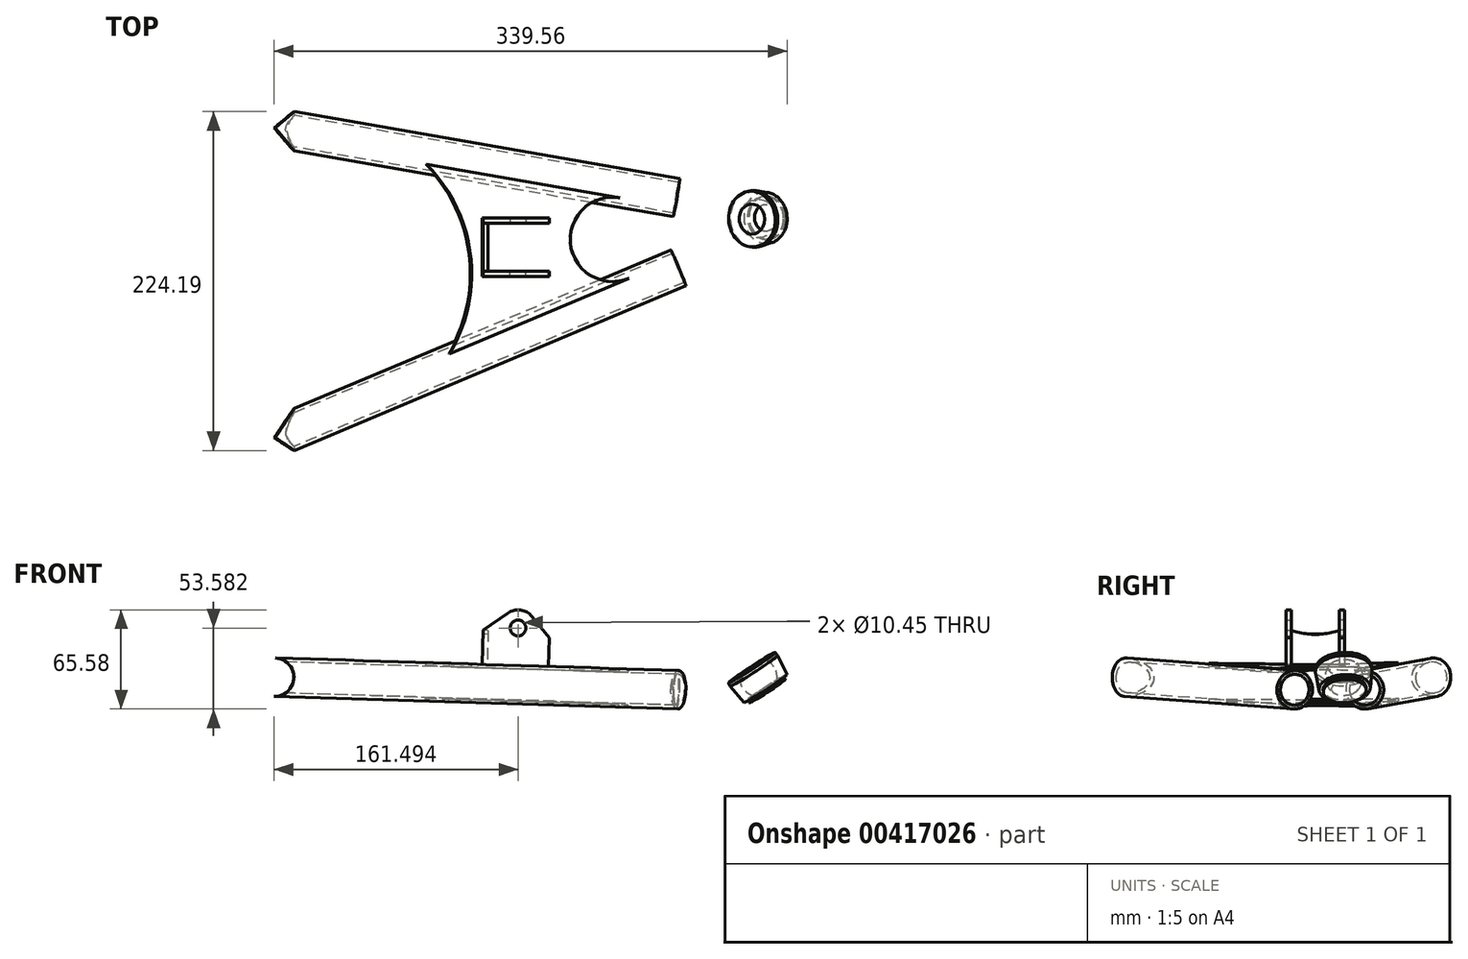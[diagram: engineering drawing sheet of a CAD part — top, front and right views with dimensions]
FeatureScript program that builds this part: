
annotation { "Feature Type Name" : "Feature", "Feature Type Description" : "" }
export const myFeature = defineFeature(function(context is Context, id is Id, definition is map)
    precondition{}
    {
        {
            var Q0;
            Q0=qCreatedBy(makeId("Front.planeOp"),FACE);
            var sketch = newSketch(context, id + "F0", { "sketchPlane" : qUnion([Q0])});
            skLineSegment(sketch, "E0", {"start": v(0, 0) * mm, "end": v(319.69, -10) * mm});
            skLineSegment(sketch, "E1", {"start": v(319.69, -10) * mm, "end": v(320, 0) * mm});
            skLineSegment(sketch, "E2", {"start": v(159.92, -5) * mm, "end": v(161.1, 32.48) * mm, "construction": true});
            skSolve(sketch);
        }
        {
            var Q0;
            Q0=qCreatedBy(makeId("Front.planeOp"),FACE);
            var Q1;
            Q1=sQuery(id+"F0.wireOp",EDGE,"E0");
            cPlane(context, id + "F1", {"entities" : qUnion([Q0, Q1]), "cplaneType" : CPlaneType.LINE_ANGLE, "offset" : 25.4 * mm, "angle" : 90 * degree, "width" : 152.4 * mm, "height" : 152.4 * mm});
        }
        {
            var Q0;
            Q0=qCreatedBy(id+"F1.planeOp",FACE);
            var sketch = newSketch(context, id + "F2", { "sketchPlane" : qUnion([Q0])});
            skLineSegment(sketch, "E3", {"start": v(0, 60) * mm, "end": v(266, 13.74) * mm});
            skLineSegment(sketch, "E4", {"start": v(345, 0) * mm, "end": v(267.35, -32.64) * mm, "construction": true});
            skLineSegment(sketch, "E5", {"start": v(266, 13.74) * mm, "end": v(345, 0) * mm, "construction": true});
            skLineSegment(sketch, "E6", {"start": v(267.35, -32.64) * mm, "end": v(0, -145) * mm});
            skLineSegment(sketch, "E7", {"start": v(0, 81) * mm, "end": v(0, 32) * mm});
            skLineSegment(sketch, "E8", {"start": v(0, -161) * mm, "end": v(0, -112) * mm});
            skLineSegment(sketch, "E9", {"start": v(160, -3) * mm, "end": v(160, -35) * mm, "construction": true});
            skLineSegment(sketch, "E10", {"start": v(160, -19) * mm, "end": v(41.18, -19) * mm, "construction": true});
            skSolve(sketch);
        }
        {
            var Q0;
            Q0=qCreatedBy(makeId("Top.planeOp"),FACE);
            var sketch = newSketch(context, id + "F3", { "sketchPlane" : qUnion([Q0])});
            skLineSegment(sketch, "E11", {"start": v(319.09, 10.43) * mm, "end": v(320.91, -10.43) * mm});
            skSolve(sketch);
        }
        {
            var Q0;
            Q0=qCreatedBy(makeId("Top.planeOp"),FACE);
            var Q1;
            Q1=sQuery(id+"F3.wireOp",EDGE,"E11");
            cPlane(context, id + "F4", {"entities" : qUnion([Q0, Q1]), "cplaneType" : CPlaneType.LINE_ANGLE, "offset" : 25.4 * mm, "angle" : 33 * degree, "width" : 152.4 * mm, "height" : 152.4 * mm});
        }
        {
            var Q0;
            Q0=qCreatedBy(id+"F4.planeOp",FACE);
            var sketch = newSketch(context, id + "F5", { "sketchPlane" : qUnion([Q0])});
            skLineSegment(sketch, "E12", {"start": v(280.63, -1.23) * mm, "end": v(256.98, 1.23) * mm});
            skSolve(sketch);
        }
        {
            var Q0;
            Q0=qCreatedBy(id+"F4.planeOp",FACE);
            var Q1;
            Q1 = qBodyType(qCreatedBy(id + "F5" ,EDGE), BodyType.WIRE);
            cPlane(context, id + "F6", {"entities" : qUnion([Q0, Q1]), "cplaneType" : CPlaneType.LINE_ANGLE, "offset" : 25.4 * mm, "angle" : 90 * degree, "width" : 152.4 * mm, "height" : 152.4 * mm});
        }
        {
            var Q0;
            Q0=qCreatedBy(id+"F6.planeOp",FACE);
            var sketch = newSketch(context, id + "F7", { "sketchPlane" : qUnion([Q0])});
            skLineSegment(sketch, "E13", {"start": v(-312.78, 9.24) * mm, "end": v(-324.78, -9.24) * mm, "construction": true});
            skLineSegment(sketch, "E14", {"start": v(-324.77, -9.23) * mm, "end": v(-336.72, -1.46) * mm});
            skLineSegment(sketch, "E15", {"start": v(-336.72, -1.46) * mm, "end": v(-335.64, 0.21) * mm});
            skLineSegment(sketch, "E16", {"start": v(-335.64, 0.21) * mm, "end": v(-337.94, 1.71) * mm});
            skLineSegment(sketch, "E17", {"start": v(-337.94, 1.71) * mm, "end": v(-331.76, 14.39) * mm});
            skLineSegment(sketch, "E18", {"start": v(-331.76, 14.39) * mm, "end": v(-330.14, 16.32) * mm});
            skLineSegment(sketch, "E19", {"start": v(-330.14, 16.32) * mm, "end": v(-323.08, 11.74) * mm});
            skArc(sketch, "E20", {"start": v(-323.08, 11.74) * mm, "mid": v(-329.78, 5.95) * mm, "end": v(-330.96, -2.82) * mm});
            skLineSegment(sketch, "E21", {"start": v(-330.96, -2.82) * mm, "end": v(-323.68, -7.55) * mm});
            skLineSegment(sketch, "E22", {"start": v(-323.68, -7.55) * mm, "end": v(-324.77, -9.23) * mm});
            skSolve(sketch);
        }
        {
            var Q0;
            Q0=makeQuery(id+"F7.imprint","IMPRINT",FACE,{"disambiguationData":[TD([[makeQuery(id+"F7.imprint","IMPRINT",EDGE,{"derivedFrom":sQuery(id+"F7.wireOp",EDGE,"E14")}),-1.0]])]});
            var Q1;
            Q1=sQuery(id+"F7.wireOp",EDGE,"E13");
            revolve(context, id + "F8", {"entities" : qUnion([Q0]), "axis" : qUnion([Q1]), "revolveType" : RevolveType.FULL});
        }
        {
            var Q0;
            Q0=qCreatedBy(makeId("Front.planeOp"),FACE);
            var sketch = newSketch(context, id + "F9", { "sketchPlane" : qUnion([Q0])});
            skCircle(sketch, "E23", {"center": v(0, 0) * mm, "radius": 12.75 * mm});
            skCircle(sketch, "E24", {"center": v(0, 0) * mm, "radius": 10.5 * mm});
            skLineSegment(sketch, "E25", {"start": v(24, 12) * mm, "end": v(188.38, 6.87) * mm, "construction": true});
            skLineSegment(sketch, "E26", {"start": v(24.34, -13.52) * mm, "end": v(189.13, -18.67) * mm, "construction": true});
            skSolve(sketch);
        }
        {
            var Q0;
            Q0 = qSketchRegion(id + "F9", true);
            var Q1;
            Q1=sQuery(id+"F2.wireOp",VERTEX,"E8.start");
            var Q2;
            Q2=sQuery(id+"F2.wireOp",VERTEX,"E7.start");
            extrude(context, id + "F10", {"entities" : qUnion([Q0]), "endBound" : BoundingType.UP_TO_VERTEX, "endBoundEntityVertex" : qUnion([Q1]), "depth" : 25.4 * mm, "hasSecondDirection" : true, "secondDirectionBound" : BoundingType.UP_TO_VERTEX, "secondDirectionOppositeDirection" : true, "secondDirectionBoundEntityVertex" : qUnion([Q2]), "secondDirectionDepth" : 25.4 * mm});
        }
        {
            var Q0;
            Q0=qCreatedBy(makeId("Top.planeOp"),FACE);
            var sketch = newSketch(context, id + "F11", { "sketchPlane" : qUnion([Q0])});
            skLineSegment(sketch, "E27.bottom", {"start": v(-116.55, 32) * mm, "end": v(116.55, 32) * mm});
            skLineSegment(sketch, "E27.top", {"start": v(-116.55, -112) * mm, "end": v(116.55, -112) * mm});
            skLineSegment(sketch, "E27.left", {"start": v(-116.55, 32) * mm, "end": v(-116.55, -112) * mm});
            skLineSegment(sketch, "E27.right", {"start": v(116.55, 32) * mm, "end": v(116.55, -112) * mm});
            skSolve(sketch);
        }
        {
            var Q0;
            Q0 = qSketchRegion(id + "F11", true);
            extrude(context, id + "F12", {"entities" : qUnion([Q0]), "operationType" : NewBodyOperationType.REMOVE, "endBound" : BoundingType.THROUGH_ALL, "oppositeDirection" : true, "depth" : 25.4 * mm, "hasSecondDirection" : true, "secondDirectionBound" : BoundingType.THROUGH_ALL, "secondDirectionOppositeDirection" : false, "secondDirectionDepth" : 25.4 * mm});
        }
        {
            var Q0;
            Q0=sQuery(id+"F2.wireOp",EDGE,"E3");
            var Q1;
            Q1=sQuery(id+"F2.wireOp",VERTEX,"E3.start");
            cPlane(context, id + "F13", {"entities" : qUnion([Q0, Q1]), "cplaneType" : CPlaneType.LINE_POINT, "offset" : 25.4 * mm, "width" : 152.4 * mm, "height" : 152.4 * mm});
        }
        {
            var Q0;
            Q0=qCreatedBy(id+"F13.planeOp",FACE);
            var sketch = newSketch(context, id + "F14", { "sketchPlane" : qUnion([Q0])});
            skCircle(sketch, "E28", {"center": v(59.11, 0) * mm, "radius": 12.75 * mm});
            skCircle(sketch, "E29", {"center": v(59.11, 0) * mm, "radius": 10.25 * mm});
            skSolve(sketch);
        }
        {
            var Q0;
            Q0 = qSketchRegion(id + "F14", true);
            var Q1;
            Q1=sQuery(id+"F2.wireOp",VERTEX,"E5.start");
            extrude(context, id + "F15", {"entities" : qUnion([Q0]), "endBound" : BoundingType.UP_TO_VERTEX, "endBoundEntityVertex" : qUnion([Q1]), "depth" : 25.4 * mm});
        }
        {
            var Q0;
            Q0=sQuery(id+"F2.wireOp",EDGE,"E6");
            var Q1;
            Q1=sQuery(id+"F2.wireOp",VERTEX,"E6.end");
            cPlane(context, id + "F16", {"entities" : qUnion([Q0, Q1]), "cplaneType" : CPlaneType.LINE_POINT, "offset" : 25.4 * mm, "width" : 152.4 * mm, "height" : 152.4 * mm});
        }
        {
            var Q0;
            Q0=qCreatedBy(id+"F16.planeOp",FACE);
            var sketch = newSketch(context, id + "F17", { "sketchPlane" : qUnion([Q0])});
            skCircle(sketch, "E30", {"center": v(133.67, 0) * mm, "radius": 12.75 * mm});
            skCircle(sketch, "E31", {"center": v(133.67, 0) * mm, "radius": 10.25 * mm});
            skSolve(sketch);
        }
        {
            var Q0;
            Q0 = qSketchRegion(id + "F17", true);
            var Q1;
            Q1=sQuery(id+"F2.wireOp",VERTEX,"E6.start");
            extrude(context, id + "F18", {"entities" : qUnion([Q0]), "endBound" : BoundingType.UP_TO_VERTEX, "oppositeDirection" : true, "endBoundEntityVertex" : qUnion([Q1]), "depth" : 25.4 * mm});
        }
        {
            var Q0;
            Q0=qCreatedBy(makeId("Front.planeOp"),FACE);
            var sketch = newSketch(context, id + "F19", { "sketchPlane" : qUnion([Q0])});
            skCircle(sketch, "E32.0", {"center": v(0, 0) * mm, "radius": 12.75 * mm});
            skSolve(sketch);
        }
        {
            var Q0;
            Q0 = qSketchRegion(id + "F19", true);
            extrude(context, id + "F20", {"entities" : qUnion([Q0]), "operationType" : NewBodyOperationType.REMOVE, "endBound" : BoundingType.THROUGH_ALL, "oppositeDirection" : true, "depth" : 25.4 * mm, "hasSecondDirection" : true, "secondDirectionBound" : BoundingType.THROUGH_ALL, "secondDirectionOppositeDirection" : false, "secondDirectionDepth" : 25.4 * mm});
        }
        {
            var Q0;
            Q0=qCreatedBy(id+"F1.planeOp",FACE);
            var Q1;
            Q1=sQuery(id+"F9.wireOp",VERTEX,"E25.start");
            cPlane(context, id + "F21", {"entities" : qUnion([Q0, Q1]), "cplaneType" : CPlaneType.PLANE_POINT, "offset" : 25.4 * mm, "width" : 152.4 * mm, "height" : 152.4 * mm});
        }
        {
            var Q0;
            Q0=qCreatedBy(id+"F21.planeOp",FACE);
            var sketch = newSketch(context, id + "F22", { "sketchPlane" : qUnion([Q0])});
            skArc(sketch, "E33", {"start": v(115.4, -89.45) * mm, "mid": v(129.23, -24.07) * mm, "end": v(100, 36.01) * mm});
            skLineSegment(sketch, "E34", {"start": v(100, 36.01) * mm, "end": v(115.4, -89.45) * mm, "construction": true});
            skLineSegment(sketch, "E35", {"start": v(130, -36.62) * mm, "end": v(130, 140.27) * mm, "construction": true});
            skArc(sketch, "E36", {"start": v(228.08, 13.74) * mm, "mid": v(195.52, -16.94) * mm, "end": v(234.12, -39.55) * mm});
            skLineSegment(sketch, "E37", {"start": v(100, 36.01) * mm, "end": v(228.08, 13.74) * mm});
            skLineSegment(sketch, "E38", {"start": v(115.4, -89.45) * mm, "end": v(234.12, -39.55) * mm});
            skSolve(sketch);
        }
        {
            var Q0;
            Q0 = qSketchRegion(id + "F22", true);
            extrude(context, id + "F23", {"entities" : qUnion([Q0]), "oppositeDirection" : true, "depth" : 2 * mm});
        }
        {
            var Q0;
            Q0=makeQuery(id+"F23.opExtrude","SWEPT_BODY",BODY,{"disambiguationData":[OSD([sQuery(id+"F22.wireOp",EDGE,"E33"),sQuery(id+"F22.wireOp",EDGE,"E36"),sQuery(id+"F22.wireOp",EDGE,"E37"),sQuery(id+"F22.wireOp",EDGE,"E38")])]});
            var Q1;
            Q1=qCreatedBy(id+"F1.planeOp",FACE);
            mirror(context, id + "F24", {"entities" : qUnion([Q0]), "mirrorPlane" : qUnion([Q1])});
        }
        {
            var Q0;
            Q0=sQuery(id+"F2.wireOp",EDGE,"E9");
            cPoint(context, id + "F25", {"entities" : qUnion([Q0]), "parameter" : 0.5});
        }
        {
            var Q0;
            Q0=qCreatedBy(makeId("Front.planeOp"),FACE);
            var Q1;
            Q1 = qCreatedBy(id + "F25" ,VERTEX);
            cPlane(context, id + "F26", {"entities" : qUnion([Q0, Q1]), "cplaneType" : CPlaneType.PLANE_POINT, "offset" : 25.4 * mm, "width" : 152.4 * mm, "height" : 152.4 * mm});
        }
        {
            var Q0;
            Q0=qCreatedBy(id+"F26.planeOp",FACE);
            var Q1;
            Q1=sQuery(id+"F2.wireOp",VERTEX,"E9.end");
            cPlane(context, id + "F27", {"entities" : qUnion([Q0, Q1]), "cplaneType" : CPlaneType.PLANE_POINT, "offset" : 25.4 * mm, "width" : 152.4 * mm, "height" : 152.4 * mm});
        }
        {
            var Q0;
            Q0=qCreatedBy(id+"F27.planeOp",FACE);
            var sketch = newSketch(context, id + "F28", { "sketchPlane" : qUnion([Q0])});
            skCircle(sketch, "E39", {"center": v(161.1, 32.48) * mm, "radius": 5.22 * mm});
            skArc(sketch, "E40", {"start": v(170.36, 40.1) * mm, "mid": v(162.7, 44.37) * mm, "end": v(154.2, 42.3) * mm});
            skLineSegment(sketch, "E41", {"start": v(154.2, 42.3) * mm, "end": v(138.03, 30.95) * mm});
            skLineSegment(sketch, "E42", {"start": v(170.36, 40.1) * mm, "end": v(181.9, 26.08) * mm});
            skLineSegment(sketch, "E43", {"start": v(181.9, 26.08) * mm, "end": v(181.31, 7.09) * mm});
            skLineSegment(sketch, "E44", {"start": v(138.03, 30.95) * mm, "end": v(137.33, 8.46) * mm});
            skLineSegment(sketch, "E45", {"start": v(137.33, 8.46) * mm, "end": v(181.31, 7.09) * mm});
            skSolve(sketch);
        }
        {
            var Q0;
            Q0 = qSketchRegion(id + "F28", true);
            extrude(context, id + "F29", {"entities" : qUnion([Q0]), "depth" : 3.25 * mm});
        }
        {
            var Q0;
            Q0=makeQuery(id+"F29.opExtrude","SWEPT_BODY",BODY,{"disambiguationData":[OSD([sQuery(id+"F28.wireOp",EDGE,"E39"),sQuery(id+"F28.wireOp",EDGE,"E40"),sQuery(id+"F28.wireOp",EDGE,"E41"),sQuery(id+"F28.wireOp",EDGE,"E42"),sQuery(id+"F28.wireOp",EDGE,"E43"),sQuery(id+"F28.wireOp",EDGE,"E44"),sQuery(id+"F28.wireOp",EDGE,"E45")])]});
            var Q1;
            Q1=qCreatedBy(id+"F26.planeOp",FACE);
            mirror(context, id + "F30", {"entities" : qUnion([Q0]), "mirrorPlane" : qUnion([Q1])});
        }
        {
            var Q0;
            Q0=makeQuery(id+"F29.opExtrude","SWEPT_FACE",FACE,{"disambiguationData":[OSD([sQuery(id+"F28.wireOp",EDGE,"E44")])]});
            var sketch = newSketch(context, id + "F31", { "sketchPlane" : qUnion([Q0])});
            skLineSegment(sketch, "E46", {"start": v(3, 12.75) * mm, "end": v(35, 12.75) * mm});
            skLineSegment(sketch, "E47.0", {"start": v(3, 35.25) * mm, "end": v(3, 12.75) * mm});
            skLineSegment(sketch, "E48.0", {"start": v(35, 35.25) * mm, "end": v(35, 12.75) * mm});
            skArc(sketch, "E49", {"start": v(3, 35.25) * mm, "mid": v(19, 32.75) * mm, "end": v(35, 35.25) * mm});
            skSolve(sketch);
        }
        {
            var Q0;
            Q0 = qSketchRegion(id + "F31", true);
            extrude(context, id + "F32", {"entities" : qUnion([Q0]), "operationType" : NewBodyOperationType.ADD, "oppositeDirection" : true, "depth" : 3.25 * mm});
        }
    });
